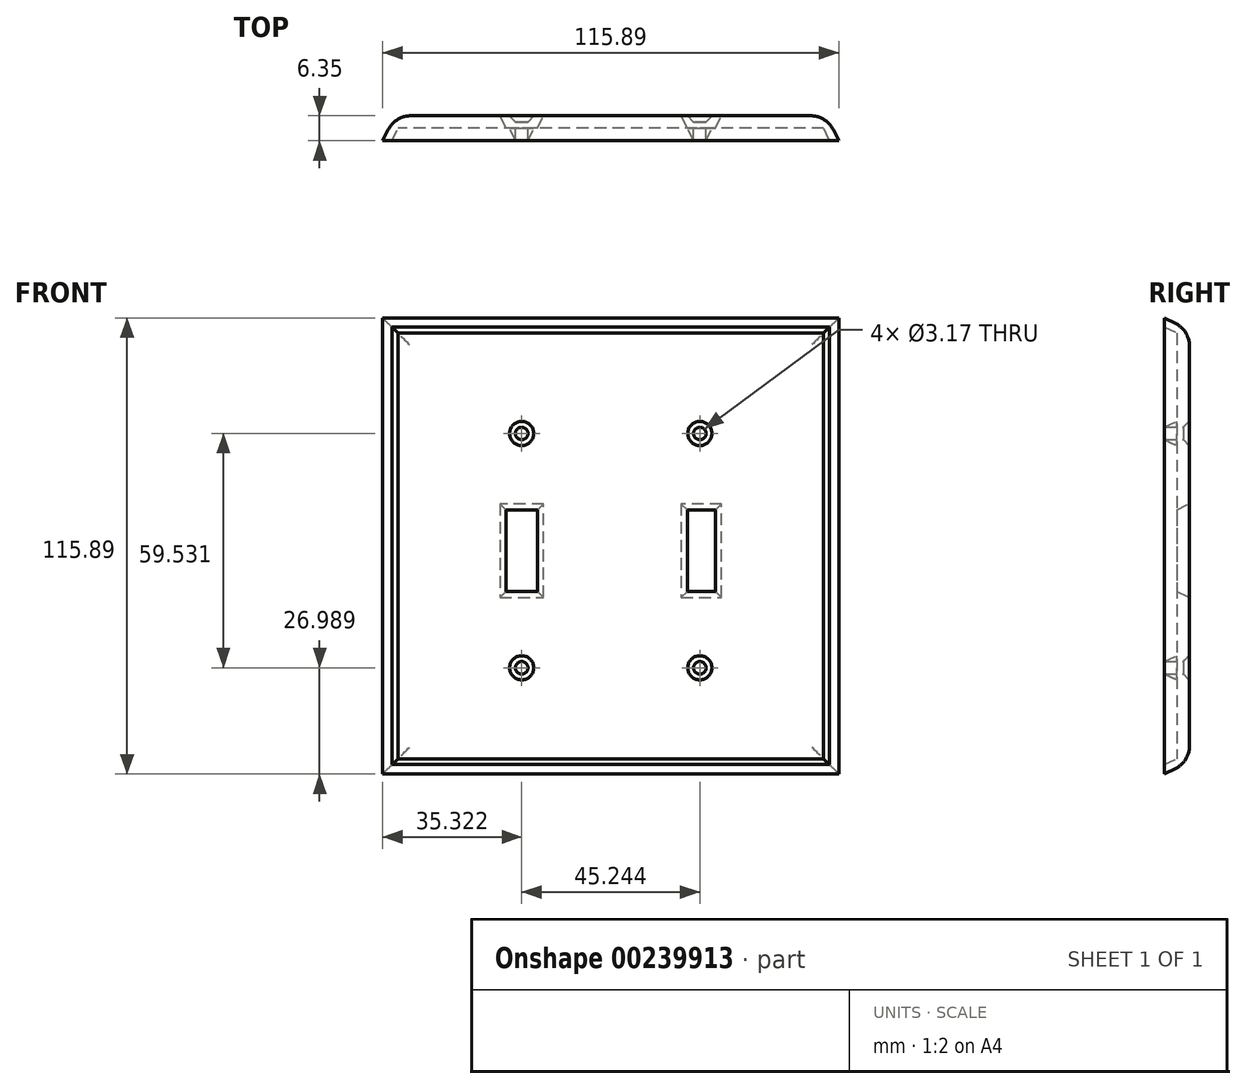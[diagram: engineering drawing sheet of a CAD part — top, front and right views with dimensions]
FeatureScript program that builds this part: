
annotation { "Feature Type Name" : "Feature", "Feature Type Description" : "" }
export const myFeature = defineFeature(function(context is Context, id is Id, definition is map)
    precondition{}
    {
        {
            var Q0;
            Q0=qCreatedBy(makeId("Front.planeOp"),FACE);
            var sketch = newSketch(context, id + "F0", { "sketchPlane" : qUnion([Q0])});
            skLineSegment(sketch, "E0.bottom", {"start": v(58.74, 61.04) * mm, "end": v(-57.15, 61.04) * mm});
            skLineSegment(sketch, "E0.top", {"start": v(58.74, -54.85) * mm, "end": v(-57.15, -54.85) * mm});
            skLineSegment(sketch, "E0.left", {"start": v(58.74, 61.04) * mm, "end": v(58.74, -54.85) * mm});
            skLineSegment(sketch, "E0.right", {"start": v(-57.15, 61.04) * mm, "end": v(-57.15, -54.85) * mm});
            skLineSegment(sketch, "E1", {"start": v(-16.27, 13.81) * mm, "end": v(-27.38, 13.81) * mm});
            skLineSegment(sketch, "E2", {"start": v(-27.38, 13.81) * mm, "end": v(-27.38, -10) * mm});
            skLineSegment(sketch, "E3", {"start": v(-27.38, -10) * mm, "end": v(-16.27, -10) * mm});
            skLineSegment(sketch, "E4", {"start": v(-16.27, -10) * mm, "end": v(-16.27, 13.81) * mm});
            skLineSegment(sketch, "E5", {"start": v(18.65, -10) * mm, "end": v(18.65, 13.81) * mm});
            skLineSegment(sketch, "E6", {"start": v(18.65, 13.81) * mm, "end": v(28.97, 13.81) * mm});
            skLineSegment(sketch, "E7", {"start": v(28.97, 13.81) * mm, "end": v(28.97, -10) * mm});
            skLineSegment(sketch, "E8", {"start": v(28.97, -10) * mm, "end": v(18.65, -10) * mm});
            skPoint(sketch, "E9", {"position": v(-21.83, 31.67) * mm});
            skPoint(sketch, "E10", {"position": v(23.42, 31.67) * mm});
            skPoint(sketch, "E11", {"position": v(-21.83, -27.86) * mm});
            skPoint(sketch, "E12", {"position": v(23.42, -27.86) * mm});
            skLineSegment(sketch, "E13", {"start": v(-57.15, 57.86) * mm, "end": v(58.74, 57.86) * mm});
            skLineSegment(sketch, "E14", {"start": v(55.56, 61.04) * mm, "end": v(55.56, -54.85) * mm});
            skLineSegment(sketch, "E15", {"start": v(58.74, -51.67) * mm, "end": v(-57.15, -51.67) * mm});
            skLineSegment(sketch, "E16", {"start": v(-53.97, -54.85) * mm, "end": v(-53.98, 61.04) * mm});
            skSolve(sketch);
        }
        {
            var Q0;
            Q0=makeQuery(id+"F0.imprint","IMPRINT",FACE,{"disambiguationData":[TD([[makeQuery(id+"F0.imprint","IMPRINT",EDGE,{"derivedFrom":sQuery(id+"F0.wireOp",EDGE,"E1")}),-1.0]])]});
            extrude(context, id + "F1", {"entities" : qUnion([Q0]), "depth" : 6.35 * mm, "hasDraft" : true, "draftAngle" : 26.57 * degree});
        }
        {
            var Q0;
            Q0=sQuery(id+"F0.wireOp",VERTEX,"E9");
            var Q1;
            Q1=makeQuery(id+"F1.opExtrude","SWEPT_BODY",BODY,{"disambiguationData":[OSD([sQuery(id+"F0.wireOp",EDGE,"E0.bottom"),sQuery(id+"F0.wireOp",EDGE,"E0.top"),sQuery(id+"F0.wireOp",EDGE,"E0.left"),sQuery(id+"F0.wireOp",EDGE,"E0.right"),sQuery(id+"F0.wireOp",EDGE,"E1"),sQuery(id+"F0.wireOp",EDGE,"E2"),sQuery(id+"F0.wireOp",EDGE,"E3"),sQuery(id+"F0.wireOp",EDGE,"E4"),sQuery(id+"F0.wireOp",EDGE,"E5"),sQuery(id+"F0.wireOp",EDGE,"E6"),sQuery(id+"F0.wireOp",EDGE,"E7"),sQuery(id+"F0.wireOp",EDGE,"E8")])]});
            hole(context, id + "F2", {"style" : HoleStyle.C_SINK, "endStyle" : HoleEndStyle.BLIND, "oppositeDirection" : true, "holeDiameter" : 3.17 * mm, "cSinkDiameter" : 6.35 * mm, "cSinkAngle" : 90 * degree, "holeDepth" : 9.52 * mm, "tappedDepth" : 12.7 * mm, "tapClearance" : 3, "startFromSketch" : true, "locations" : qUnion([Q0]), "scope" : qUnion([Q1])});
        }
        {
            var Q0;
            Q0=sQuery(id+"F0.wireOp",VERTEX,"E10");
            var Q1;
            Q1=makeQuery(id+"F1.opExtrude","SWEPT_BODY",BODY,{"disambiguationData":[OSD([sQuery(id+"F0.wireOp",EDGE,"E0.bottom"),sQuery(id+"F0.wireOp",EDGE,"E0.top"),sQuery(id+"F0.wireOp",EDGE,"E0.left"),sQuery(id+"F0.wireOp",EDGE,"E0.right"),sQuery(id+"F0.wireOp",EDGE,"E1"),sQuery(id+"F0.wireOp",EDGE,"E2"),sQuery(id+"F0.wireOp",EDGE,"E3"),sQuery(id+"F0.wireOp",EDGE,"E4"),sQuery(id+"F0.wireOp",EDGE,"E5"),sQuery(id+"F0.wireOp",EDGE,"E6"),sQuery(id+"F0.wireOp",EDGE,"E7"),sQuery(id+"F0.wireOp",EDGE,"E8")])]});
            hole(context, id + "F3", {"style" : HoleStyle.C_SINK, "endStyle" : HoleEndStyle.BLIND, "oppositeDirection" : true, "holeDiameter" : 3.17 * mm, "cSinkDiameter" : 6.35 * mm, "cSinkAngle" : 90 * degree, "holeDepth" : 9.52 * mm, "tappedDepth" : 12.7 * mm, "tapClearance" : 3, "startFromSketch" : true, "locations" : qUnion([Q0]), "scope" : qUnion([Q1])});
        }
        {
            var Q0;
            Q0=sQuery(id+"F0.wireOp",VERTEX,"E12");
            var Q1;
            Q1=makeQuery(id+"F1.opExtrude","SWEPT_BODY",BODY,{"disambiguationData":[OSD([sQuery(id+"F0.wireOp",EDGE,"E0.bottom"),sQuery(id+"F0.wireOp",EDGE,"E0.top"),sQuery(id+"F0.wireOp",EDGE,"E0.left"),sQuery(id+"F0.wireOp",EDGE,"E0.right"),sQuery(id+"F0.wireOp",EDGE,"E1"),sQuery(id+"F0.wireOp",EDGE,"E2"),sQuery(id+"F0.wireOp",EDGE,"E3"),sQuery(id+"F0.wireOp",EDGE,"E4"),sQuery(id+"F0.wireOp",EDGE,"E5"),sQuery(id+"F0.wireOp",EDGE,"E6"),sQuery(id+"F0.wireOp",EDGE,"E7"),sQuery(id+"F0.wireOp",EDGE,"E8")])]});
            hole(context, id + "F4", {"style" : HoleStyle.C_SINK, "endStyle" : HoleEndStyle.BLIND, "oppositeDirection" : true, "holeDiameter" : 3.17 * mm, "cSinkDiameter" : 6.35 * mm, "cSinkAngle" : 90 * degree, "holeDepth" : 9.52 * mm, "tappedDepth" : 12.7 * mm, "tapClearance" : 3, "startFromSketch" : true, "locations" : qUnion([Q0]), "scope" : qUnion([Q1])});
        }
        {
            var Q0;
            Q0=sQuery(id+"F0.wireOp",VERTEX,"E11");
            var Q1;
            Q1=makeQuery(id+"F1.opExtrude","SWEPT_BODY",BODY,{"disambiguationData":[OSD([sQuery(id+"F0.wireOp",EDGE,"E0.bottom"),sQuery(id+"F0.wireOp",EDGE,"E0.top"),sQuery(id+"F0.wireOp",EDGE,"E0.left"),sQuery(id+"F0.wireOp",EDGE,"E0.right"),sQuery(id+"F0.wireOp",EDGE,"E1"),sQuery(id+"F0.wireOp",EDGE,"E2"),sQuery(id+"F0.wireOp",EDGE,"E3"),sQuery(id+"F0.wireOp",EDGE,"E4"),sQuery(id+"F0.wireOp",EDGE,"E5"),sQuery(id+"F0.wireOp",EDGE,"E6"),sQuery(id+"F0.wireOp",EDGE,"E7"),sQuery(id+"F0.wireOp",EDGE,"E8")])]});
            hole(context, id + "F5", {"style" : HoleStyle.C_SINK, "endStyle" : HoleEndStyle.BLIND, "oppositeDirection" : true, "holeDiameter" : 3.17 * mm, "cSinkDiameter" : 6.35 * mm, "cSinkAngle" : 90 * degree, "holeDepth" : 9.52 * mm, "tappedDepth" : 12.7 * mm, "tapClearance" : 3, "startFromSketch" : true, "locations" : qUnion([Q0]), "scope" : qUnion([Q1])});
        }
        {
            var Q0;
            Q0=makeQuery(id+"F1.opExtrude","CAP_EDGE",EDGE,{"disambiguationData":[OSD([sQuery(id+"F0.wireOp",EDGE,"E13")])],"isStart":true});
            var Q1;
            Q1=makeQuery(id+"F1.opExtrude","CAP_EDGE",EDGE,{"disambiguationData":[OSD([sQuery(id+"F0.wireOp",EDGE,"E14")])],"isStart":true});
            var Q2;
            Q2=makeQuery(id+"F1.opExtrude","CAP_EDGE",EDGE,{"disambiguationData":[OSD([sQuery(id+"F0.wireOp",EDGE,"E16")])],"isStart":true});
            var Q3;
            Q3=makeQuery(id+"F1.opExtrude","CAP_EDGE",EDGE,{"disambiguationData":[OSD([sQuery(id+"F0.wireOp",EDGE,"E15")])],"isStart":true});
            fillet(context, id + "F6", {"entities" : qUnion([Q0, Q1, Q2, Q3]), "radius" : 6.35 * mm, "tangentPropagation" : true, "allowEdgeOverflow" : false});
        }
        {
            var Q0;
            Q0=makeQuery(id+"F1.opExtrude","CAP_FACE",FACE,{"disambiguationData":[OSD([sQuery(id+"F0.wireOp",EDGE,"E1"),sQuery(id+"F0.wireOp",EDGE,"E2"),sQuery(id+"F0.wireOp",EDGE,"E3"),sQuery(id+"F0.wireOp",EDGE,"E4"),sQuery(id+"F0.wireOp",EDGE,"E5"),sQuery(id+"F0.wireOp",EDGE,"E6"),sQuery(id+"F0.wireOp",EDGE,"E7"),sQuery(id+"F0.wireOp",EDGE,"E8"),sQuery(id+"F0.wireOp",EDGE,"E13"),sQuery(id+"F0.wireOp",EDGE,"E14"),sQuery(id+"F0.wireOp",EDGE,"E15"),sQuery(id+"F0.wireOp",EDGE,"E16")])],"isStart":false});
            var sketch = newSketch(context, id + "F7", { "sketchPlane" : qUnion([Q0])});
            skLineSegment(sketch, "E17", {"start": v(-57.15, 58.66) * mm, "end": v(58.74, 58.66) * mm});
            skLineSegment(sketch, "E18", {"start": v(-54.77, 61.04) * mm, "end": v(-54.77, -54.85) * mm});
            skLineSegment(sketch, "E19", {"start": v(56.36, 61.04) * mm, "end": v(56.36, -54.85) * mm});
            skLineSegment(sketch, "E20", {"start": v(58.74, -52.47) * mm, "end": v(-57.15, -52.47) * mm});
            skSolve(sketch);
        }
        {
            var Q0;
            {var subQ5=sQuery(id+"F0.wireOp",EDGE,"E1");Q0=makeQuery(id+"F7.imprint","IMPRINT",FACE,{"disambiguationData":[TD([[makeQuery(id+"F7.imprint","IMPRINT",EDGE,{"derivedFrom":makeQuery(id+"F1.opExtrude","CAP_EDGE",EDGE,{"disambiguationData":[OSD([subQ5])],"isStart":false})}),-1.0]])]});}
            extrude(context, id + "F8", {"entities" : qUnion([Q0]), "operationType" : NewBodyOperationType.REMOVE, "oppositeDirection" : true, "depth" : 3.17 * mm, "hasDraft" : true, "draftAngle" : 25 * degree, "draftPullDirection" : true});
        }
    });
